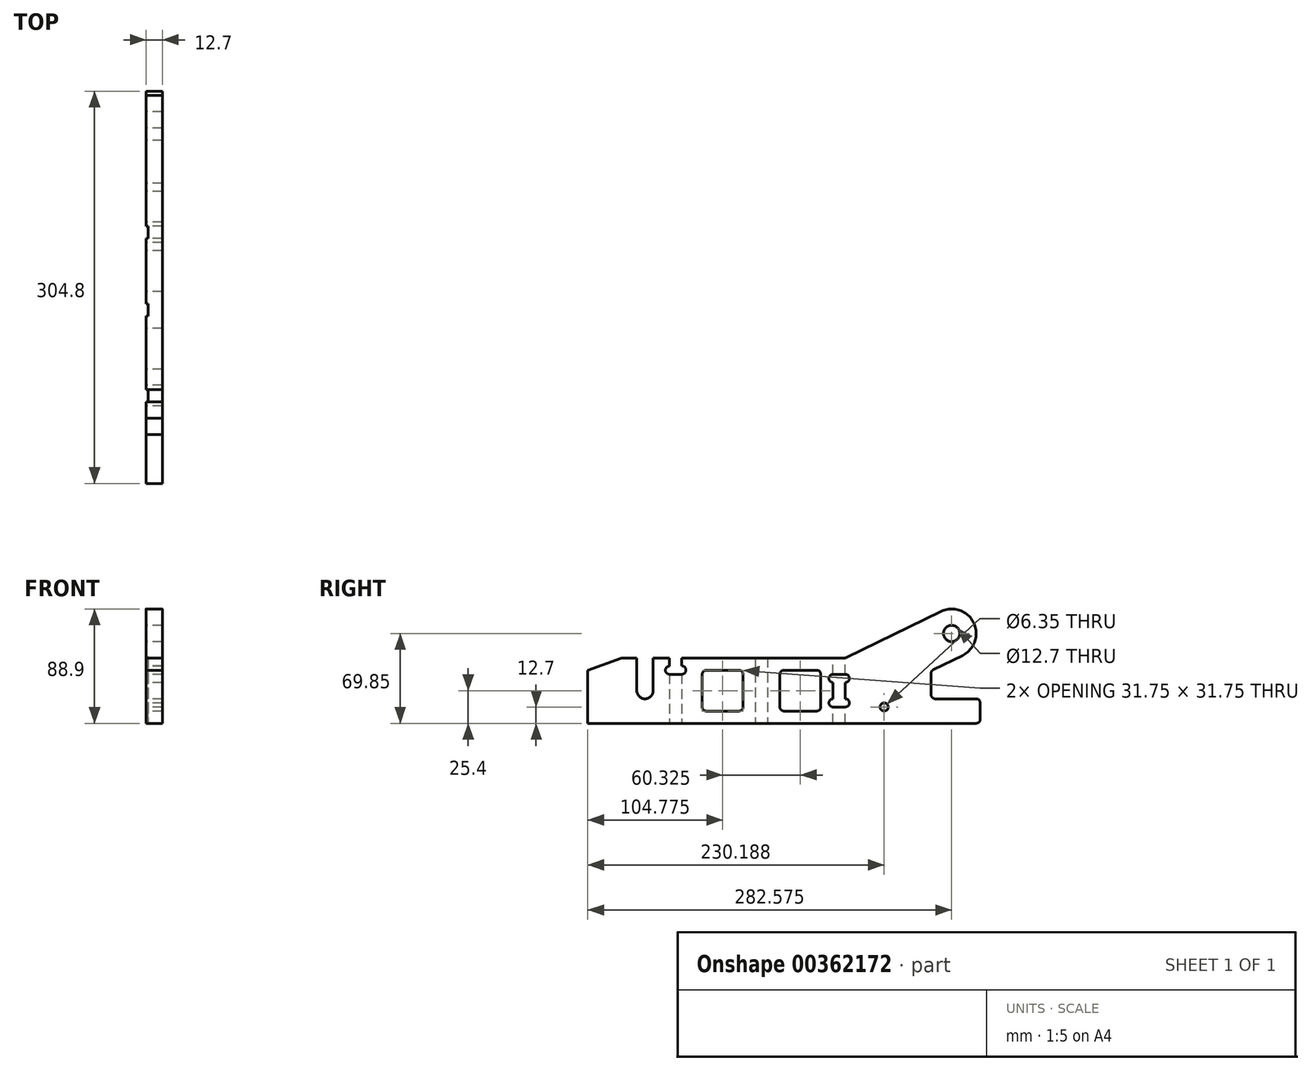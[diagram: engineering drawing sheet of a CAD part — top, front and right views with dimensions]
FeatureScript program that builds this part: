
annotation { "Feature Type Name" : "Feature", "Feature Type Description" : "" }
export const myFeature = defineFeature(function(context is Context, id is Id, definition is map)
    precondition{}
    {
        {
            var Q0;
            Q0=qCreatedBy(makeId("Right.planeOp"),FACE);
            var sketch = newSketch(context, id + "F0", { "sketchPlane" : qUnion([Q0])});
            skLineSegment(sketch, "E0", {"start": v(0, 0) * mm, "end": v(0, 41.28) * mm});
            skLineSegment(sketch, "E1", {"start": v(0, 41.28) * mm, "end": v(26.72, 50.8) * mm});
            skLineSegment(sketch, "E2", {"start": v(26.72, 50.8) * mm, "end": v(200.03, 50.8) * mm});
            skLineSegment(sketch, "E3", {"start": v(200.03, 50.8) * mm, "end": v(274.23, 86.97) * mm});
            skArc(sketch, "E4", {"start": v(290.92, 52.73) * mm, "mid": v(299.7, 78.2) * mm, "end": v(274.23, 86.97) * mm});
            skLineSegment(sketch, "E5", {"start": v(0, 0) * mm, "end": v(304.8, 0) * mm});
            skLineSegment(sketch, "E6", {"start": v(304.8, 0) * mm, "end": v(304.8, 19.05) * mm});
            skLineSegment(sketch, "E7", {"start": v(304.8, 19.05) * mm, "end": v(266.7, 19.05) * mm});
            skLineSegment(sketch, "E8", {"start": v(266.7, 19.05) * mm, "end": v(266.7, 40.92) * mm});
            skLineSegment(sketch, "E9", {"start": v(266.7, 40.92) * mm, "end": v(290.92, 52.73) * mm});
            skPoint(sketch, "E10", {"position": v(44.45, 25.4) * mm});
            skLineSegment(sketch, "E11", {"start": v(44.45, 25.4) * mm, "end": v(44.45, 50.8) * mm, "construction": true});
            skLineSegment(sketch, "E12", {"start": v(44.45, 25.4) * mm, "end": v(44.45, 0) * mm, "construction": true});
            skCircle(sketch, "E13", {"center": v(44.45, 25.4) * mm, "radius": 38.1 * mm, "construction": true});
            skLineSegment(sketch, "E14", {"start": v(38.1, 50.8) * mm, "end": v(38.1, 25.4) * mm});
            skArc(sketch, "E15", {"start": v(38.1, 25.4) * mm, "mid": v(44.45, 19.05) * mm, "end": v(50.8, 25.4) * mm});
            skLineSegment(sketch, "E16", {"start": v(50.8, 25.4) * mm, "end": v(50.8, 50.8) * mm});
            skLineSegment(sketch, "E17", {"start": v(44.45, 38.1) * mm, "end": v(63.5, 38.1) * mm, "construction": true});
            skLineSegment(sketch, "E18", {"start": v(63.5, 38.1) * mm, "end": v(73.02, 38.1) * mm});
            skLineSegment(sketch, "E19", {"start": v(73.03, 50.8) * mm, "end": v(73.03, 44.62) * mm});
            skLineSegment(sketch, "E20", {"start": v(63.5, 50.8) * mm, "end": v(63.5, 44.45) * mm});
            skArc(sketch, "E21", {"start": v(63.5, 44.45) * mm, "mid": v(60.32, 41.27) * mm, "end": v(63.5, 38.1) * mm});
            skArc(sketch, "E22", {"start": v(73.03, 38.1) * mm, "mid": v(76.28, 41.36) * mm, "end": v(73.02, 44.62) * mm});
            skLineSegment(sketch, "E23", {"start": v(130.18, 50.8) * mm, "end": v(130.18, 0) * mm});
            skLineSegment(sketch, "E24", {"start": v(44.45, -12.7) * mm, "end": v(304.8, -12.7) * mm, "construction": true});
            skLineSegment(sketch, "E25", {"start": v(139.7, 50.8) * mm, "end": v(139.7, 0) * mm});
            skCircle(sketch, "E26", {"center": v(230.19, 12.7) * mm, "radius": 25.4 * mm, "construction": true});
            skCircle(sketch, "E27", {"center": v(230.19, 12.7) * mm, "radius": 3.18 * mm});
            skLineSegment(sketch, "E28", {"start": v(298.45, 19.05) * mm, "end": v(298.45, 9.53) * mm, "construction": true});
            skLineSegment(sketch, "E29", {"start": v(298.45, 9.53) * mm, "end": v(298.45, 0) * mm, "construction": true});
            skLineSegment(sketch, "E30", {"start": v(285.75, 9.53) * mm, "end": v(298.45, 9.53) * mm, "construction": true});
            skCircle(sketch, "E31", {"center": v(282.58, 69.85) * mm, "radius": 6.35 * mm});
            skLineSegment(sketch, "E32", {"start": v(200.03, 38.1) * mm, "end": v(190.5, 38.1) * mm});
            skLineSegment(sketch, "E33", {"start": v(190.5, 12.7) * mm, "end": v(200.03, 12.7) * mm});
            skLineSegment(sketch, "E34", {"start": v(190.5, 38.1) * mm, "end": v(190.5, 50.8) * mm, "construction": true});
            skLineSegment(sketch, "E35", {"start": v(190.5, 50.8) * mm, "end": v(200.03, 50.8) * mm, "construction": true});
            skLineSegment(sketch, "E36", {"start": v(190.5, 12.7) * mm, "end": v(190.5, 0) * mm, "construction": true});
            skArc(sketch, "E37", {"start": v(190.5, 19.05) * mm, "mid": v(187.33, 15.87) * mm, "end": v(190.5, 12.7) * mm});
            skArc(sketch, "E38", {"start": v(190.5, 38.1) * mm, "mid": v(187.33, 34.92) * mm, "end": v(190.5, 31.75) * mm});
            skLineSegment(sketch, "E39", {"start": v(190.5, 31.75) * mm, "end": v(190.5, 19.05) * mm});
            skArc(sketch, "E40", {"start": v(200.03, 12.7) * mm, "mid": v(203.2, 15.87) * mm, "end": v(200.03, 19.05) * mm});
            skArc(sketch, "E41", {"start": v(200.03, 31.75) * mm, "mid": v(203.2, 34.92) * mm, "end": v(200.03, 38.1) * mm});
            skLineSegment(sketch, "E42", {"start": v(200.03, 19.05) * mm, "end": v(200.03, 31.75) * mm});
            skLineSegment(sketch, "E43", {"start": v(200.03, 38.1) * mm, "end": v(200.03, 50.8) * mm, "construction": true});
            skLineSegment(sketch, "E44", {"start": v(63.5, 38.1) * mm, "end": v(63.5, 0) * mm});
            skLineSegment(sketch, "E45", {"start": v(73.02, 38.1) * mm, "end": v(73.02, 0) * mm});
            skCircle(sketch, "E46", {"center": v(282.58, 69.85) * mm, "radius": 76.2 * mm, "construction": true});
            skLineSegment(sketch, "E47", {"start": v(256.99, 141.62) * mm, "end": v(31.66, 61.29) * mm, "construction": true});
            skLineSegment(sketch, "E48", {"start": v(31.66, 61.29) * mm, "end": v(0, 50) * mm, "construction": true});
            skLineSegment(sketch, "E49", {"start": v(282.58, 69.85) * mm, "end": v(279.8, 75.56) * mm, "construction": true});
            skLineSegment(sketch, "E50", {"start": v(282.58, 69.85) * mm, "end": v(285.36, 64.14) * mm, "construction": true});
            skPoint(sketch, "E51", {"position": v(288.14, 58.43) * mm});
            skLineSegment(sketch, "E52", {"start": v(285.36, 64.14) * mm, "end": v(288.14, 58.43) * mm, "construction": true});
            skLineSegment(sketch, "E53", {"start": v(282.58, 69.85) * mm, "end": v(276.87, 67.07) * mm, "construction": true});
            skLineSegment(sketch, "E54", {"start": v(276.87, 67.07) * mm, "end": v(271.16, 64.28) * mm, "construction": true});
            skLineSegment(sketch, "E55", {"start": v(282.58, 69.85) * mm, "end": v(288.28, 72.63) * mm, "construction": true});
            skLineSegment(sketch, "E56", {"start": v(288.28, 72.63) * mm, "end": v(294, 75.42) * mm, "construction": true});
            skPoint(sketch, "E57", {"position": v(271.16, 64.28) * mm});
            skPoint(sketch, "E58", {"position": v(294, 75.42) * mm});
            skLineSegment(sketch, "E59", {"start": v(260.35, 92.14) * mm, "end": v(260.35, 0) * mm, "construction": true});
            skLineSegment(sketch, "E60", {"start": v(260.35, 0) * mm, "end": v(266.7, 0) * mm, "construction": true});
            skLineSegment(sketch, "E61", {"start": v(266.7, 0) * mm, "end": v(266.7, 50.33) * mm, "construction": true});
            skLineSegment(sketch, "E62", {"start": v(263.53, 20.64) * mm, "end": v(263.53, 41.28) * mm, "construction": true});
            skLineSegment(sketch, "E63", {"start": v(263.53, 20.64) * mm, "end": v(263.53, 0) * mm, "construction": true});
            skPoint(sketch, "E64", {"position": v(263.53, 30.96) * mm});
            skPoint(sketch, "E65", {"position": v(263.53, 10.32) * mm});
            skLineSegment(sketch, "E66", {"start": v(260.35, 20.64) * mm, "end": v(266.7, 20.64) * mm, "construction": true});
            skLineSegment(sketch, "E67", {"start": v(266.7, 41.28) * mm, "end": v(260.35, 41.28) * mm, "construction": true});
            skLineSegment(sketch, "E68", {"start": v(200.03, 12.7) * mm, "end": v(200.03, 0) * mm, "construction": true});
            skLineSegment(sketch, "E69", {"start": v(230.19, 12.7) * mm, "end": v(200.03, 12.7) * mm, "construction": true});
            skPoint(sketch, "E70", {"position": v(285.75, 9.53) * mm});
            skPoint(sketch, "E71", {"position": v(298.45, 9.53) * mm});
            skLineSegment(sketch, "E72", {"start": v(230.19, 12.7) * mm, "end": v(260.35, 12.7) * mm, "construction": true});
            skLineSegment(sketch, "E73.bottom", {"start": v(120.65, 41.28) * mm, "end": v(88.9, 41.28) * mm});
            skLineSegment(sketch, "E73.top", {"start": v(120.65, 9.53) * mm, "end": v(88.9, 9.53) * mm});
            skLineSegment(sketch, "E73.left", {"start": v(120.65, 41.28) * mm, "end": v(120.65, 9.53) * mm});
            skLineSegment(sketch, "E73.right", {"start": v(88.9, 41.27) * mm, "end": v(88.9, 9.53) * mm});
            skLineSegment(sketch, "E74.bottom", {"start": v(149.22, 41.27) * mm, "end": v(180.98, 41.27) * mm});
            skLineSegment(sketch, "E74.top", {"start": v(149.23, 9.53) * mm, "end": v(180.98, 9.53) * mm});
            skLineSegment(sketch, "E74.left", {"start": v(149.23, 41.27) * mm, "end": v(149.23, 9.53) * mm});
            skLineSegment(sketch, "E74.right", {"start": v(180.98, 41.28) * mm, "end": v(180.98, 9.53) * mm});
            skLineSegment(sketch, "E75", {"start": v(120.65, 41.28) * mm, "end": v(120.65, 50.8) * mm, "construction": true});
            skLineSegment(sketch, "E76", {"start": v(120.65, 41.28) * mm, "end": v(130.18, 41.28) * mm, "construction": true});
            skLineSegment(sketch, "E77", {"start": v(149.22, 41.27) * mm, "end": v(139.7, 41.27) * mm, "construction": true});
            skLineSegment(sketch, "E78", {"start": v(149.23, 41.27) * mm, "end": v(149.23, 50.8) * mm, "construction": true});
            skLineSegment(sketch, "E79", {"start": v(120.65, 9.53) * mm, "end": v(120.65, 0) * mm, "construction": true});
            skSolve(sketch);
        }
        {
            var Q0;
            {var subQ0=sQuery(id+"F0.wireOp",EDGE,"E23");Q0=makeQuery(id+"F0.imprint","IMPRINT",FACE,{"disambiguationData":[TD([[makeQuery(id+"F0.imprint","IMPRINT",EDGE,{"derivedFrom":subQ0}),1.0]])]});}
            var Q1;
            {var subQ2=sQuery(id+"F0.wireOp",EDGE,"E3");Q1=makeQuery(id+"F0.imprint","IMPRINT",FACE,{"disambiguationData":[TD([[makeQuery(id+"F0.imprint","IMPRINT",EDGE,{"derivedFrom":subQ2}),-1.0]])]});}
            var Q2;
            {var subQ0=sQuery(id+"F0.wireOp",EDGE,"E19");Q2=makeQuery(id+"F0.imprint","IMPRINT",FACE,{"disambiguationData":[TD([[makeQuery(id+"F0.imprint","IMPRINT",EDGE,{"derivedFrom":subQ0}),1.0]])]});}
            var Q3;
            Q3=makeQuery(id+"F0.imprint","IMPRINT",FACE,{"disambiguationData":[TD([[makeQuery(id+"F0.imprint","IMPRINT",EDGE,{"derivedFrom":sQuery(id+"F0.wireOp",EDGE,"E18")}),-1.0]])]});
            var Q4;
            {var subQ6=sQuery(id+"F0.wireOp",EDGE,"E0");Q4=makeQuery(id+"F0.imprint","IMPRINT",FACE,{"disambiguationData":[TD([[makeQuery(id+"F0.imprint","IMPRINT",EDGE,{"derivedFrom":subQ6}),-1.0]])]});}
            extrude(context, id + "F1", {"entities" : qUnion([Q0, Q1, Q2, Q3, Q4]), "depth" : 12.7 * mm});
        }
        {
            var Q0;
            Q0=makeQuery(id+"F1.opExtrude","SWEPT_EDGE",EDGE,{"disambiguationData":[OSD([sQuery(id+"F0.wireOp",EDGE,"E2"),sQuery(id+"F0.wireOp",EDGE,"E3")])]});
            var Q1;
            Q1=makeQuery(id+"F1.opExtrude","SWEPT_EDGE",EDGE,{"disambiguationData":[OSD([sQuery(id+"F0.wireOp",EDGE,"E8"),sQuery(id+"F0.wireOp",EDGE,"E9")])]});
            var Q2;
            Q2=makeQuery(id+"F1.opExtrude","SWEPT_EDGE",EDGE,{"disambiguationData":[OSD([sQuery(id+"F0.wireOp",EDGE,"E7"),sQuery(id+"F0.wireOp",EDGE,"E8")])]});
            var Q3;
            Q3=makeQuery(id+"F1.opExtrude","SWEPT_EDGE",EDGE,{"disambiguationData":[OSD([sQuery(id+"F0.wireOp",EDGE,"E6"),sQuery(id+"F0.wireOp",EDGE,"E7")])]});
            var Q4;
            Q4=makeQuery(id+"F1.opExtrude","SWEPT_EDGE",EDGE,{"disambiguationData":[OSD([sQuery(id+"F0.wireOp",EDGE,"E5"),sQuery(id+"F0.wireOp",EDGE,"E6")])]});
            var Q5;
            Q5=makeQuery(id+"F1.opExtrude","SWEPT_EDGE",EDGE,{"disambiguationData":[OSD([sQuery(id+"F0.wireOp",EDGE,"E74.bottom"),sQuery(id+"F0.wireOp",EDGE,"E74.left")])]});
            var Q6;
            Q6=makeQuery(id+"F1.opExtrude","SWEPT_EDGE",EDGE,{"disambiguationData":[OSD([sQuery(id+"F0.wireOp",EDGE,"E73.bottom"),sQuery(id+"F0.wireOp",EDGE,"E73.right")])]});
            var Q7;
            Q7=makeQuery(id+"F1.opExtrude","SWEPT_EDGE",EDGE,{"disambiguationData":[OSD([sQuery(id+"F0.wireOp",EDGE,"E74.top"),sQuery(id+"F0.wireOp",EDGE,"E74.right")])]});
            var Q8;
            Q8=makeQuery(id+"F1.opExtrude","SWEPT_EDGE",EDGE,{"disambiguationData":[OSD([sQuery(id+"F0.wireOp",EDGE,"E74.bottom"),sQuery(id+"F0.wireOp",EDGE,"E74.right")])]});
            var Q9;
            Q9=makeQuery(id+"F1.opExtrude","SWEPT_EDGE",EDGE,{"disambiguationData":[OSD([sQuery(id+"F0.wireOp",EDGE,"E73.bottom"),sQuery(id+"F0.wireOp",EDGE,"E73.left")])]});
            var Q10;
            Q10=makeQuery(id+"F1.opExtrude","SWEPT_EDGE",EDGE,{"disambiguationData":[OSD([sQuery(id+"F0.wireOp",EDGE,"E74.top"),sQuery(id+"F0.wireOp",EDGE,"E74.left")])]});
            var Q11;
            Q11=makeQuery(id+"F1.opExtrude","SWEPT_EDGE",EDGE,{"disambiguationData":[OSD([sQuery(id+"F0.wireOp",EDGE,"E73.top"),sQuery(id+"F0.wireOp",EDGE,"E73.right")])]});
            var Q12;
            Q12=makeQuery(id+"F1.opExtrude","SWEPT_EDGE",EDGE,{"disambiguationData":[OSD([sQuery(id+"F0.wireOp",EDGE,"E73.top"),sQuery(id+"F0.wireOp",EDGE,"E73.left")])]});
            var Q13;
            Q13=makeQuery(id+"F1.opExtrude","SWEPT_EDGE",EDGE,{"disambiguationData":[OSD([sQuery(id+"F0.wireOp",EDGE,"E1"),sQuery(id+"F0.wireOp",EDGE,"E2")])]});
            fillet(context, id + "F2", {"entities" : qUnion([Q0, Q1, Q2, Q3, Q4, Q5, Q6, Q7, Q8, Q9, Q10, Q11, Q12, Q13]), "radius" : 3.17 * mm, "tangentPropagation" : true, "allowEdgeOverflow" : false});
        }
        {
            var Q0;
            Q0=makeQuery(id+"F1.opExtrude","CAP_FACE",FACE,{"disambiguationData":[OSD([sQuery(id+"F0.wireOp",EDGE,"E0"),sQuery(id+"F0.wireOp",EDGE,"E1"),sQuery(id+"F0.wireOp",EDGE,"E2"),sQuery(id+"F0.wireOp",EDGE,"E3"),sQuery(id+"F0.wireOp",EDGE,"E4"),sQuery(id+"F0.wireOp",EDGE,"E5"),sQuery(id+"F0.wireOp",EDGE,"E6"),sQuery(id+"F0.wireOp",EDGE,"E7"),sQuery(id+"F0.wireOp",EDGE,"E8"),sQuery(id+"F0.wireOp",EDGE,"E9"),sQuery(id+"F0.wireOp",EDGE,"E14"),sQuery(id+"F0.wireOp",EDGE,"E15"),sQuery(id+"F0.wireOp",EDGE,"E16"),sQuery(id+"F0.wireOp",EDGE,"E18"),sQuery(id+"F0.wireOp",EDGE,"E19"),sQuery(id+"F0.wireOp",EDGE,"E20"),sQuery(id+"F0.wireOp",EDGE,"E21"),sQuery(id+"F0.wireOp",EDGE,"E22"),sQuery(id+"F0.wireOp",EDGE,"E27"),sQuery(id+"F0.wireOp",EDGE,"1B4OWH7D-hY2x-AemJ-kr1P-dbijIKMEHeJH"),sQuery(id+"F0.wireOp",EDGE,"vXDJeEpz-HHiL-fvMT-sxGg-cfHU6cQA9n6z"),sQuery(id+"F0.wireOp",EDGE,"E31"),sQuery(id+"F0.wireOp",EDGE,"E32"),sQuery(id+"F0.wireOp",EDGE,"E33"),sQuery(id+"F0.wireOp",EDGE,"E37"),sQuery(id+"F0.wireOp",EDGE,"E38"),sQuery(id+"F0.wireOp",EDGE,"E39"),sQuery(id+"F0.wireOp",EDGE,"E40"),sQuery(id+"F0.wireOp",EDGE,"E41"),sQuery(id+"F0.wireOp",EDGE,"E42")])],"isStart":true});
            var sketch = newSketch(context, id + "F3", { "sketchPlane" : qUnion([Q0])});
            skLineSegment(sketch, "E80.bottom", {"start": v(-73.02, 38.1) * mm, "end": v(-63.5, 38.1) * mm});
            skLineSegment(sketch, "E80.top", {"start": v(-73.03, 0) * mm, "end": v(-63.5, 0) * mm});
            skLineSegment(sketch, "E80.left", {"start": v(-73.03, 38.1) * mm, "end": v(-73.03, 0) * mm});
            skLineSegment(sketch, "E80.right", {"start": v(-63.5, 38.1) * mm, "end": v(-63.5, 0) * mm});
            skLineSegment(sketch, "E81.bottom", {"start": v(-190.5, 0) * mm, "end": v(-200.03, 0) * mm});
            skLineSegment(sketch, "E81.top", {"start": v(-190.5, 52.94) * mm, "end": v(-200.03, 52.94) * mm});
            skLineSegment(sketch, "E81.left", {"start": v(-190.5, 0) * mm, "end": v(-190.5, 52.94) * mm});
            skLineSegment(sketch, "E81.right", {"start": v(-200.03, 0) * mm, "end": v(-200.03, 52.94) * mm});
            skSolve(sketch);
        }
        {
            var Q0;
            {var subQ0=sQuery(id+"F3.wireOp",EDGE,"E81.bottom");Q0=makeQuery(id+"F3.imprint","IMPRINT",FACE,{"disambiguationData":[TD([[makeQuery(id+"F3.imprint","IMPRINT",EDGE,{"derivedFrom":subQ0}),-1.0]])]});}
            var Q1;
            Q1=makeQuery(id+"F1.opExtrude","CAP_FACE",FACE,{"disambiguationData":[OSD([sQuery(id+"F0.wireOp",EDGE,"E0"),sQuery(id+"F0.wireOp",EDGE,"E1"),sQuery(id+"F0.wireOp",EDGE,"E2"),sQuery(id+"F0.wireOp",EDGE,"E3"),sQuery(id+"F0.wireOp",EDGE,"E4"),sQuery(id+"F0.wireOp",EDGE,"E5"),sQuery(id+"F0.wireOp",EDGE,"E6"),sQuery(id+"F0.wireOp",EDGE,"E7"),sQuery(id+"F0.wireOp",EDGE,"E8"),sQuery(id+"F0.wireOp",EDGE,"E9"),sQuery(id+"F0.wireOp",EDGE,"E14"),sQuery(id+"F0.wireOp",EDGE,"E15"),sQuery(id+"F0.wireOp",EDGE,"E16"),sQuery(id+"F0.wireOp",EDGE,"E18"),sQuery(id+"F0.wireOp",EDGE,"E19"),sQuery(id+"F0.wireOp",EDGE,"E20"),sQuery(id+"F0.wireOp",EDGE,"E21"),sQuery(id+"F0.wireOp",EDGE,"E22"),sQuery(id+"F0.wireOp",EDGE,"E27"),sQuery(id+"F0.wireOp",EDGE,"1B4OWH7D-hY2x-AemJ-kr1P-dbijIKMEHeJH"),sQuery(id+"F0.wireOp",EDGE,"vXDJeEpz-HHiL-fvMT-sxGg-cfHU6cQA9n6z"),sQuery(id+"F0.wireOp",EDGE,"E31"),sQuery(id+"F0.wireOp",EDGE,"E32"),sQuery(id+"F0.wireOp",EDGE,"E33"),sQuery(id+"F0.wireOp",EDGE,"E37"),sQuery(id+"F0.wireOp",EDGE,"E38"),sQuery(id+"F0.wireOp",EDGE,"E39"),sQuery(id+"F0.wireOp",EDGE,"E40"),sQuery(id+"F0.wireOp",EDGE,"E41"),sQuery(id+"F0.wireOp",EDGE,"E42")])],"isStart":false});
            var Q2;
            {var subQ2=sQuery(id+"F0.wireOp",EDGE,"E32");var subQ3=makeQuery(id+"F1.opExtrude","CAP_EDGE",EDGE,{"disambiguationData":[OSD([subQ2])],"isStart":true});Q2=makeQuery(id+"F3.imprint","IMPRINT",FACE,{"disambiguationData":[TD([[makeQuery(id+"F3.imprint","IMPRINT",EDGE,{"derivedFrom":subQ3}),1.0]])]});}
            extrude(context, id + "F4", {"entities" : qUnion([Q0, Q1, Q2]), "operationType" : NewBodyOperationType.REMOVE, "oppositeDirection" : true, "depth" : 1.59 * mm});
        }
        {
            var Q0;
            {var subQ0=sQuery(id+"F0.wireOp",EDGE,"E23");Q0=makeQuery(id+"F0.imprint","IMPRINT",FACE,{"disambiguationData":[TD([[makeQuery(id+"F0.imprint","IMPRINT",EDGE,{"derivedFrom":subQ0}),1.0]])]});}
            extrude(context, id + "F5", {"entities" : qUnion([Q0]), "operationType" : NewBodyOperationType.REMOVE, "depth" : 1.59 * mm});
        }
        {
            var Q0;
            Q0=makeQuery(id+"F0.imprint","IMPRINT",FACE,{"disambiguationData":[TD([[makeQuery(id+"F0.imprint","IMPRINT",EDGE,{"derivedFrom":sQuery(id+"F0.wireOp",EDGE,"E18")}),-1.0]])]});
            extrude(context, id + "F6", {"entities" : qUnion([Q0]), "operationType" : NewBodyOperationType.REMOVE, "depth" : 1.59 * mm});
        }
    });
